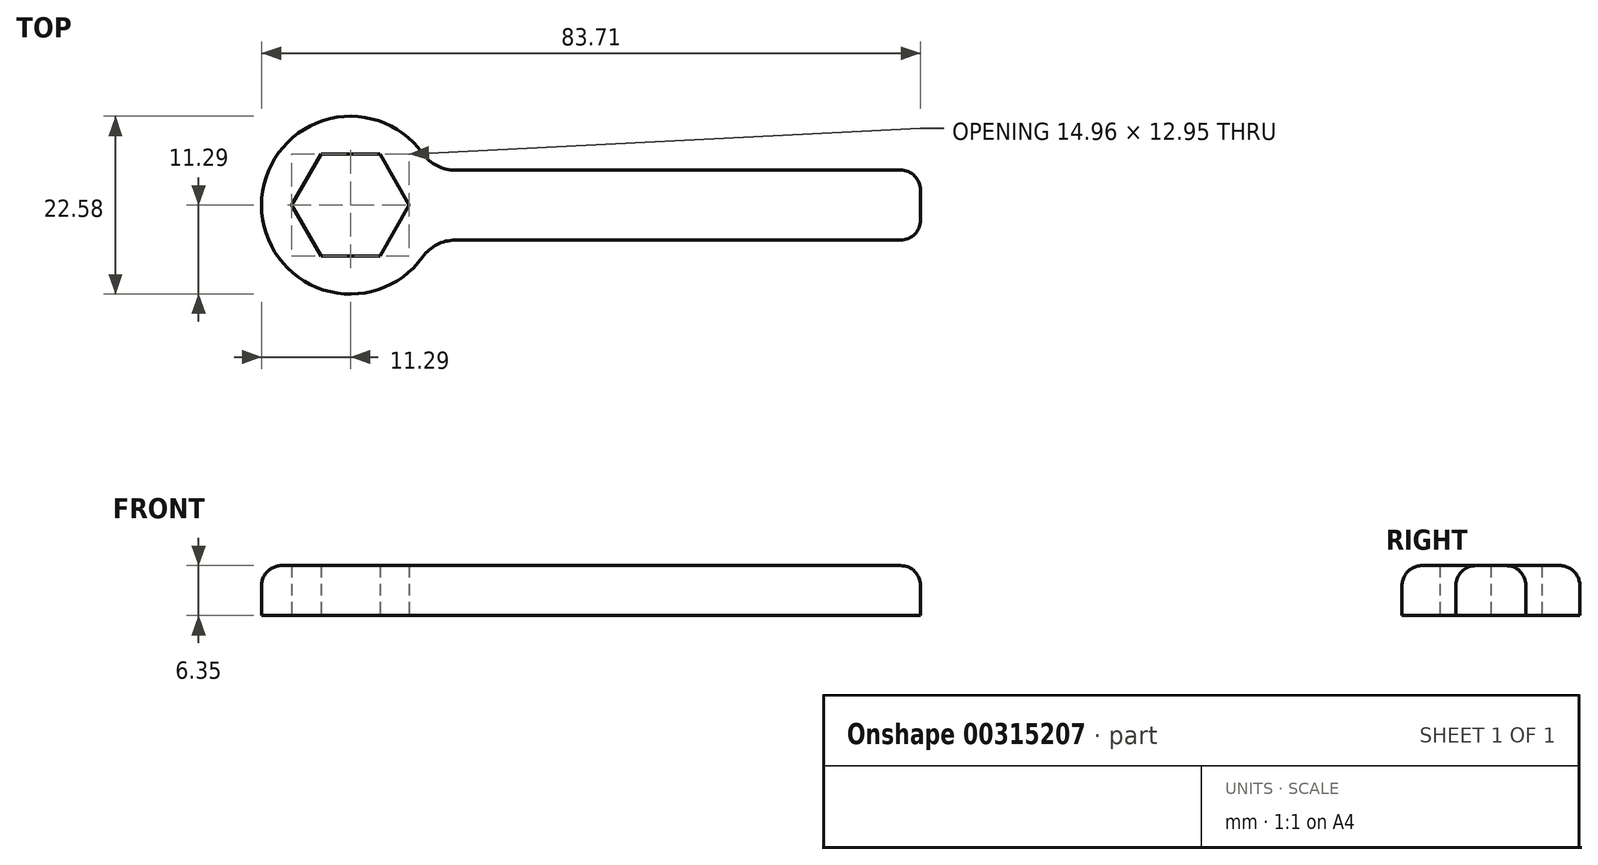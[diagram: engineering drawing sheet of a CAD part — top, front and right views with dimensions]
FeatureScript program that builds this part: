
annotation { "Feature Type Name" : "Feature", "Feature Type Description" : "" }
export const myFeature = defineFeature(function(context is Context, id is Id, definition is map)
    precondition{}
    {
        {
            var Q0;
            Q0=qCreatedBy(makeId("Top.planeOp"),FACE);
            var sketch = newSketch(context, id + "F0", { "sketchPlane" : qUnion([Q0])});
            skCircle(sketch, "E0.cCircle", {"center": v(0, 0) * mm, "radius": 6.48 * mm, "construction": true});
            skLineSegment(sketch, "E0.0", {"start": v(-3.74, -6.48) * mm, "end": v(-7.48, 0) * mm});
            skLineSegment(sketch, "E0.1", {"start": v(-7.48, 0) * mm, "end": v(-3.74, 6.48) * mm});
            skLineSegment(sketch, "E0.2", {"start": v(-3.74, 6.48) * mm, "end": v(3.74, 6.48) * mm});
            skLineSegment(sketch, "E0.3", {"start": v(3.74, 6.48) * mm, "end": v(7.48, 0) * mm});
            skLineSegment(sketch, "E0.4", {"start": v(7.48, 0) * mm, "end": v(3.74, -6.48) * mm});
            skLineSegment(sketch, "E0.5", {"start": v(3.74, -6.48) * mm, "end": v(-3.74, -6.48) * mm});
            skPoint(sketch, "E0.0.midPoint", {"position": v(-5.6, -3.24) * mm});
            skCircle(sketch, "E1", {"center": v(0, 0) * mm, "radius": 11.29 * mm});
            skPoint(sketch, "E2", {"position": v(11.29, 0) * mm});
            skLineSegment(sketch, "E3.bottom", {"start": v(8.92, 4.45) * mm, "end": v(72.42, 4.45) * mm});
            skLineSegment(sketch, "E3.top", {"start": v(8.92, -4.44) * mm, "end": v(72.42, -4.44) * mm});
            skLineSegment(sketch, "E3.left", {"start": v(8.92, 4.45) * mm, "end": v(8.92, -4.45) * mm});
            skLineSegment(sketch, "E3.right", {"start": v(72.42, 4.45) * mm, "end": v(72.42, -4.44) * mm});
            skPoint(sketch, "E4", {"position": v(8.92, 0) * mm});
            skSolve(sketch);
        }
        {
            var Q0;
            Q0=makeQuery(id+"F0.imprint","IMPRINT",FACE,{"disambiguationData":[TD([[makeQuery(id+"F0.imprint","IMPRINT",EDGE,{"derivedFrom":sQuery(id+"F0.wireOp",EDGE,"E0.0")}),1.0]])]});
            var Q1;
            {var subQ5=sQuery(id+"F0.wireOp",EDGE,"E3.left");Q1=makeQuery(id+"F0.imprint","IMPRINT",FACE,{"disambiguationData":[TD([[makeQuery(id+"F0.imprint","IMPRINT",EDGE,{"derivedFrom":subQ5}),1.0]])]});}
            var Q2;
            {var subQ5=sQuery(id+"F0.wireOp",EDGE,"E3.right");Q2=makeQuery(id+"F0.imprint","IMPRINT",FACE,{"disambiguationData":[TD([[makeQuery(id+"F0.imprint","IMPRINT",EDGE,{"derivedFrom":subQ5}),-1.0]])]});}
            extrude(context, id + "F1", {"entities" : qUnion([Q0, Q1, Q2]), "depth" : 6.35 * mm});
        }
        {
            var Q0;
            Q0=makeQuery(id+"F1.opExtrude","SWEPT_EDGE",EDGE,{"disambiguationData":[OSD([sQuery(id+"F0.wireOp",EDGE,"E1"),sQuery(id+"F0.wireOp",EDGE,"E3.top")])]});
            var Q1;
            Q1=makeQuery(id+"F1.opExtrude","SWEPT_EDGE",EDGE,{"disambiguationData":[OSD([sQuery(id+"F0.wireOp",EDGE,"E1"),sQuery(id+"F0.wireOp",EDGE,"E3.bottom")])]});
            fillet(context, id + "F2", {"entities" : qUnion([Q0, Q1]), "radius" : 5.08 * mm, "tangentPropagation" : true, "allowEdgeOverflow" : false});
        }
        {
            var Q0;
            Q0=makeQuery(id+"F1.opExtrude","SWEPT_EDGE",EDGE,{"disambiguationData":[OSD([sQuery(id+"F0.wireOp",EDGE,"E3.bottom"),sQuery(id+"F0.wireOp",EDGE,"E3.right")])]});
            var Q1;
            Q1=makeQuery(id+"F1.opExtrude","SWEPT_EDGE",EDGE,{"disambiguationData":[OSD([sQuery(id+"F0.wireOp",EDGE,"E3.top"),sQuery(id+"F0.wireOp",EDGE,"E3.right")])]});
            fillet(context, id + "F3", {"entities" : qUnion([Q0, Q1]), "radius" : 2.54 * mm, "tangentPropagation" : true, "allowEdgeOverflow" : false});
        }
        {
            var Q0;
            Q0=makeQuery(id+"F1.opExtrude","CAP_EDGE",EDGE,{"disambiguationData":[OSD([sQuery(id+"F0.wireOp",EDGE,"E3.top")])],"isStart":false});
            fillet(context, id + "F4", {"entities" : qUnion([Q0]), "radius" : 2.54 * mm, "tangentPropagation" : true, "allowEdgeOverflow" : false});
        }
    });
